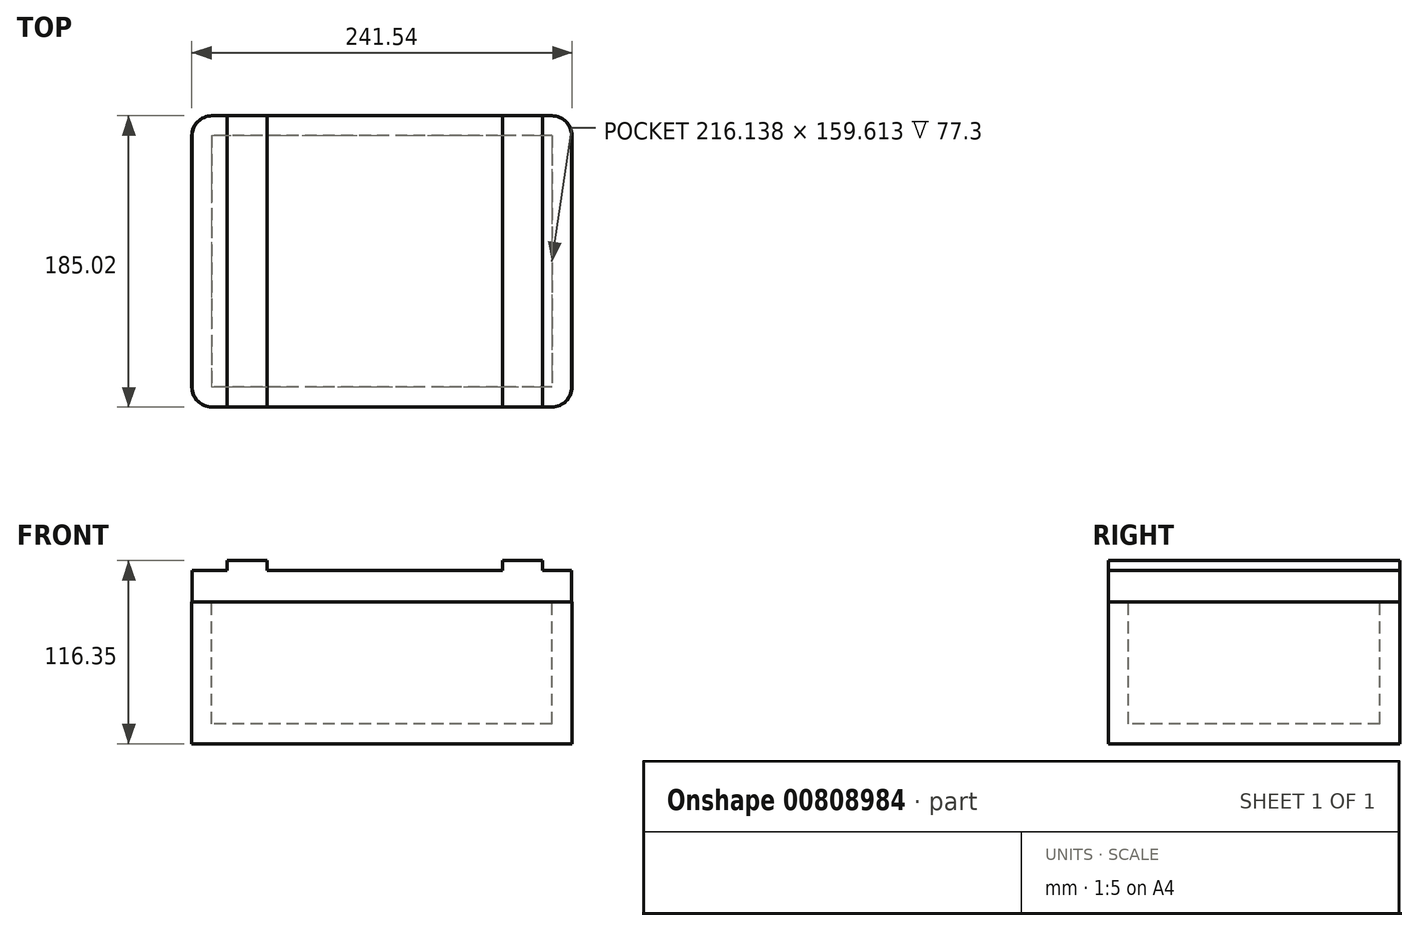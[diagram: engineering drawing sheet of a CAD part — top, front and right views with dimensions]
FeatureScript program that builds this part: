
annotation { "Feature Type Name" : "Feature", "Feature Type Description" : "" }
export const myFeature = defineFeature(function(context is Context, id is Id, definition is map)
    precondition{}
    {
        {
            var Q0;
            Q0=qCreatedBy(makeId("Top.planeOp"),FACE);
            var sketch = newSketch(context, id + "F0", { "sketchPlane" : qUnion([Q0])});
            skLineSegment(sketch, "E0.bottom", {"start": v(120.5, -92.5) * mm, "end": v(-120.5, -92.5) * mm});
            skLineSegment(sketch, "E0.top", {"start": v(120.5, 92.5) * mm, "end": v(-120.5, 92.5) * mm});
            skLineSegment(sketch, "E0.left", {"start": v(120.5, -92.5) * mm, "end": v(120.5, 92.5) * mm});
            skLineSegment(sketch, "E0.right", {"start": v(-120.5, -92.5) * mm, "end": v(-120.5, 92.5) * mm});
            skPoint(sketch, "E0.middle", {"position": v(0, 0) * mm});
            skLineSegment(sketch, "E1", {"start": v(-98.22, 92.5) * mm, "end": v(-98.22, -92.5) * mm});
            skLineSegment(sketch, "E2.0", {"start": v(-72.82, 92.5) * mm, "end": v(-72.82, -92.5) * mm});
            skLineSegment(sketch, "E3", {"start": v(102.03, 92.5) * mm, "end": v(102.03, -92.5) * mm});
            skLineSegment(sketch, "E4.0", {"start": v(76.63, 92.5) * mm, "end": v(76.63, -92.5) * mm});
            skSolve(sketch);
        }
        {
            var Q0;
            {var subQ0=sQuery(id+"F0.wireOp",EDGE,"E1");Q0=makeQuery(id+"F0.imprint","IMPRINT",FACE,{"disambiguationData":[TD([[makeQuery(id+"F0.imprint","IMPRINT",EDGE,{"derivedFrom":subQ0}),1.0]])]});}
            extrude(context, id + "F1", {"entities" : qUnion([Q0]), "depth" : 5.08 * mm, "offsetDistance" : 25.4 * mm});
        }
        {
            var Q0;
            {var subQ0=sQuery(id+"F0.wireOp",EDGE,"E0.right");Q0=makeQuery(id+"F0.imprint","IMPRINT",FACE,{"disambiguationData":[TD([[makeQuery(id+"F0.imprint","IMPRINT",EDGE,{"derivedFrom":subQ0}),-1.0]])]});}
            extrude(context, id + "F2", {"entities" : qUnion([Q0]), "oppositeDirection" : true, "depth" : 20 * mm, "offsetDistance" : 25.4 * mm});
        }
        {
            var Q0;
            {var subQ0=sQuery(id+"F0.wireOp",EDGE,"E2.0");Q0=makeQuery(id+"F0.imprint","IMPRINT",FACE,{"disambiguationData":[TD([[makeQuery(id+"F0.imprint","IMPRINT",EDGE,{"derivedFrom":subQ0}),1.0]])]});}
            extrude(context, id + "F3", {"entities" : qUnion([Q0]), "oppositeDirection" : true, "depth" : 20 * mm, "offsetDistance" : 25.4 * mm});
        }
        {
            var Q0;
            {var subQ0=sQuery(id+"F0.wireOp",EDGE,"E0.left");Q0=makeQuery(id+"F0.imprint","IMPRINT",FACE,{"disambiguationData":[TD([[makeQuery(id+"F0.imprint","IMPRINT",EDGE,{"derivedFrom":subQ0}),1.0]])]});}
            extrude(context, id + "F4", {"entities" : qUnion([Q0]), "oppositeDirection" : true, "depth" : 20 * mm, "offsetDistance" : 25.4 * mm});
        }
        {
            var Q0;
            {var subQ0=sQuery(id+"F0.wireOp",EDGE,"E3");Q0=makeQuery(id+"F0.imprint","IMPRINT",FACE,{"disambiguationData":[TD([[makeQuery(id+"F0.imprint","IMPRINT",EDGE,{"derivedFrom":subQ0}),-1.0]])]});}
            extrude(context, id + "F5", {"entities" : qUnion([Q0]), "oppositeDirection" : true, "depth" : 20 * mm, "offsetDistance" : 25.4 * mm});
        }
        {
            var Q0;
            {var subQ0=sQuery(id+"F0.wireOp",EDGE,"E1");Q0=makeQuery(id+"F0.imprint","IMPRINT",FACE,{"disambiguationData":[TD([[makeQuery(id+"F0.imprint","IMPRINT",EDGE,{"derivedFrom":subQ0}),1.0]])]});}
            extrude(context, id + "F6", {"entities" : qUnion([Q0]), "oppositeDirection" : true, "depth" : 20 * mm, "offsetDistance" : 25.4 * mm});
        }
        {
            var Q0;
            Q0=makeQuery(id+"F2.opExtrude","SWEPT_FACE",FACE,{"disambiguationData":[OSD([sQuery(id+"F0.wireOp",EDGE,"E0.bottom")])]});
            extrude(context, id + "F7", {"entities" : qUnion([Q0]), "oppositeDirection" : true, "depth" : 90 * mm, "offsetDistance" : 25.4 * mm});
        }
        {
            var Q0;
            Q0=makeQuery(id+"F3.opExtrude","CAP_FACE",FACE,{"disambiguationData":[OSD([sQuery(id+"F0.wireOp",EDGE,"E0.bottom"),sQuery(id+"F0.wireOp",EDGE,"E0.top"),sQuery(id+"F0.wireOp",EDGE,"E2.0"),sQuery(id+"F0.wireOp",EDGE,"E4.0")])],"isStart":false});
            var sketch = newSketch(context, id + "F8", { "sketchPlane" : qUnion([Q0])});
            skLineSegment(sketch, "E5.bottom", {"start": v(120.77, -92.5) * mm, "end": v(-120.77, -92.5) * mm});
            skLineSegment(sketch, "E5.top", {"start": v(120.77, 92.5) * mm, "end": v(-120.77, 92.5) * mm});
            skLineSegment(sketch, "E5.left", {"start": v(120.77, -92.5) * mm, "end": v(120.77, 92.5) * mm});
            skLineSegment(sketch, "E5.right", {"start": v(-120.77, -92.5) * mm, "end": v(-120.77, 92.5) * mm});
            skPoint(sketch, "E5.middle", {"position": v(0, 0) * mm});
            skSolve(sketch);
        }
        {
            var Q0;
            Q0 = qSketchRegion(id + "F8", true);
            extrude(context, id + "F9", {"entities" : qUnion([Q0]), "depth" : 90 * mm, "offsetDistance" : 25.4 * mm});
        }
        {
            var Q0;
            Q0=makeQuery(id+"F9.opExtrude","CAP_FACE",FACE,{"disambiguationData":[OSD([sQuery(id+"F8.wireOp",EDGE,"E5.bottom"),sQuery(id+"F8.wireOp",EDGE,"E5.top"),sQuery(id+"F8.wireOp",EDGE,"E5.left"),sQuery(id+"F8.wireOp",EDGE,"E5.right")])],"isStart":true});
            shell(context, id + "F10", {"entities" : qUnion([Q0]), "thickness" : 12.7 * mm});
        }
        {
            var Q0;
            Q0=makeQuery(id+"F9.opExtrude","SWEPT_EDGE",EDGE,{"disambiguationData":[OSD([sQuery(id+"F8.wireOp",EDGE,"E5.top"),sQuery(id+"F8.wireOp",EDGE,"E5.left")])]});
            var Q1;
            Q1=makeQuery(id+"F4.opExtrude","SWEPT_EDGE",EDGE,{"disambiguationData":[OSD([sQuery(id+"F0.wireOp",EDGE,"E0.bottom"),sQuery(id+"F0.wireOp",EDGE,"E0.left")])]});
            var Q2;
            Q2=makeQuery(id+"F9.opExtrude","SWEPT_EDGE",EDGE,{"disambiguationData":[OSD([sQuery(id+"F8.wireOp",EDGE,"E5.bottom"),sQuery(id+"F8.wireOp",EDGE,"E5.left")])]});
            var Q3;
            Q3=makeQuery(id+"F4.opExtrude","SWEPT_EDGE",EDGE,{"disambiguationData":[OSD([sQuery(id+"F0.wireOp",EDGE,"E0.top"),sQuery(id+"F0.wireOp",EDGE,"E0.left")])]});
            var Q4;
            Q4=makeQuery(id+"F9.opExtrude","SWEPT_EDGE",EDGE,{"disambiguationData":[OSD([sQuery(id+"F8.wireOp",EDGE,"E5.bottom"),sQuery(id+"F8.wireOp",EDGE,"E5.right")])]});
            var Q5;
            Q5=makeQuery(id+"F2.opExtrude","SWEPT_EDGE",EDGE,{"disambiguationData":[OSD([sQuery(id+"F0.wireOp",EDGE,"E0.top"),sQuery(id+"F0.wireOp",EDGE,"E0.right")])]});
            var Q6;
            Q6=makeQuery(id+"F9.opExtrude","SWEPT_EDGE",EDGE,{"disambiguationData":[OSD([sQuery(id+"F8.wireOp",EDGE,"E5.top"),sQuery(id+"F8.wireOp",EDGE,"E5.right")])]});
            var Q7;
            Q7=makeQuery(id+"F2.opExtrude","SWEPT_EDGE",EDGE,{"disambiguationData":[OSD([sQuery(id+"F0.wireOp",EDGE,"E0.bottom"),sQuery(id+"F0.wireOp",EDGE,"E0.right")])]});
            fillet(context, id + "F11", {"entities" : qUnion([Q0, Q1, Q2, Q3, Q4, Q5, Q6, Q7]), "radius" : 12.7 * mm, "tangentPropagation" : true, "allowEdgeOverflow" : false});
        }
        {
            var Q0;
            Q0=makeQuery(id+"F7.opExtrude","CAP_EDGE",EDGE,{"disambiguationData":[OSD([sQuery(id+"F0.wireOp",EDGE,"E0.bottom"),sQuery(id+"F0.wireOp",EDGE,"E0.right")])],"isStart":true});
            fillet(context, id + "F12", {"entities" : qUnion([Q0]), "radius" : 12.7 * mm, "tangentPropagation" : true, "allowEdgeOverflow" : false});
        }
        {
            var Q0;
            Q0=makeQuery(id+"F5.opExtrude","CAP_FACE",FACE,{"disambiguationData":[OSD([sQuery(id+"F0.wireOp",EDGE,"E0.bottom"),sQuery(id+"F0.wireOp",EDGE,"E0.top"),sQuery(id+"F0.wireOp",EDGE,"E3"),sQuery(id+"F0.wireOp",EDGE,"E4.0")])],"isStart":true});
            var sketch = newSketch(context, id + "F13", { "sketchPlane" : qUnion([Q0])});
            skSolve(sketch);
        }
        {
            var Q0;
            Q0 = qSketchRegion(id + "F13", true);
            var Q1;
            Q1=makeQuery(id+"F13.imprint","IMPRINT",FACE,{"disambiguationData":[TD([[makeQuery(id+"F13.imprint","IMPRINT",EDGE,{"derivedFrom":makeQuery(id+"F5.opExtrude","CAP_EDGE",EDGE,{"disambiguationData":[OSD([sQuery(id+"F0.wireOp",EDGE,"E0.bottom")])],"isStart":true})}),-1.0]])]});
            extrude(context, id + "F14", {"entities" : qUnion([Q0, Q1]), "operationType" : NewBodyOperationType.ADD, "depth" : 6.35 * mm, "offsetDistance" : 25.4 * mm});
        }
        {
            var Q0;
            Q0=makeQuery(id+"F6.opExtrude","CAP_FACE",FACE,{"disambiguationData":[OSD([sQuery(id+"F0.wireOp",EDGE,"E0.bottom"),sQuery(id+"F0.wireOp",EDGE,"E0.top"),sQuery(id+"F0.wireOp",EDGE,"E1"),sQuery(id+"F0.wireOp",EDGE,"E2.0")])],"isStart":true});
            extrude(context, id + "F15", {"entities" : qUnion([Q0]), "operationType" : NewBodyOperationType.ADD, "depth" : 6.35 * mm, "offsetDistance" : 25.4 * mm});
        }
    });
